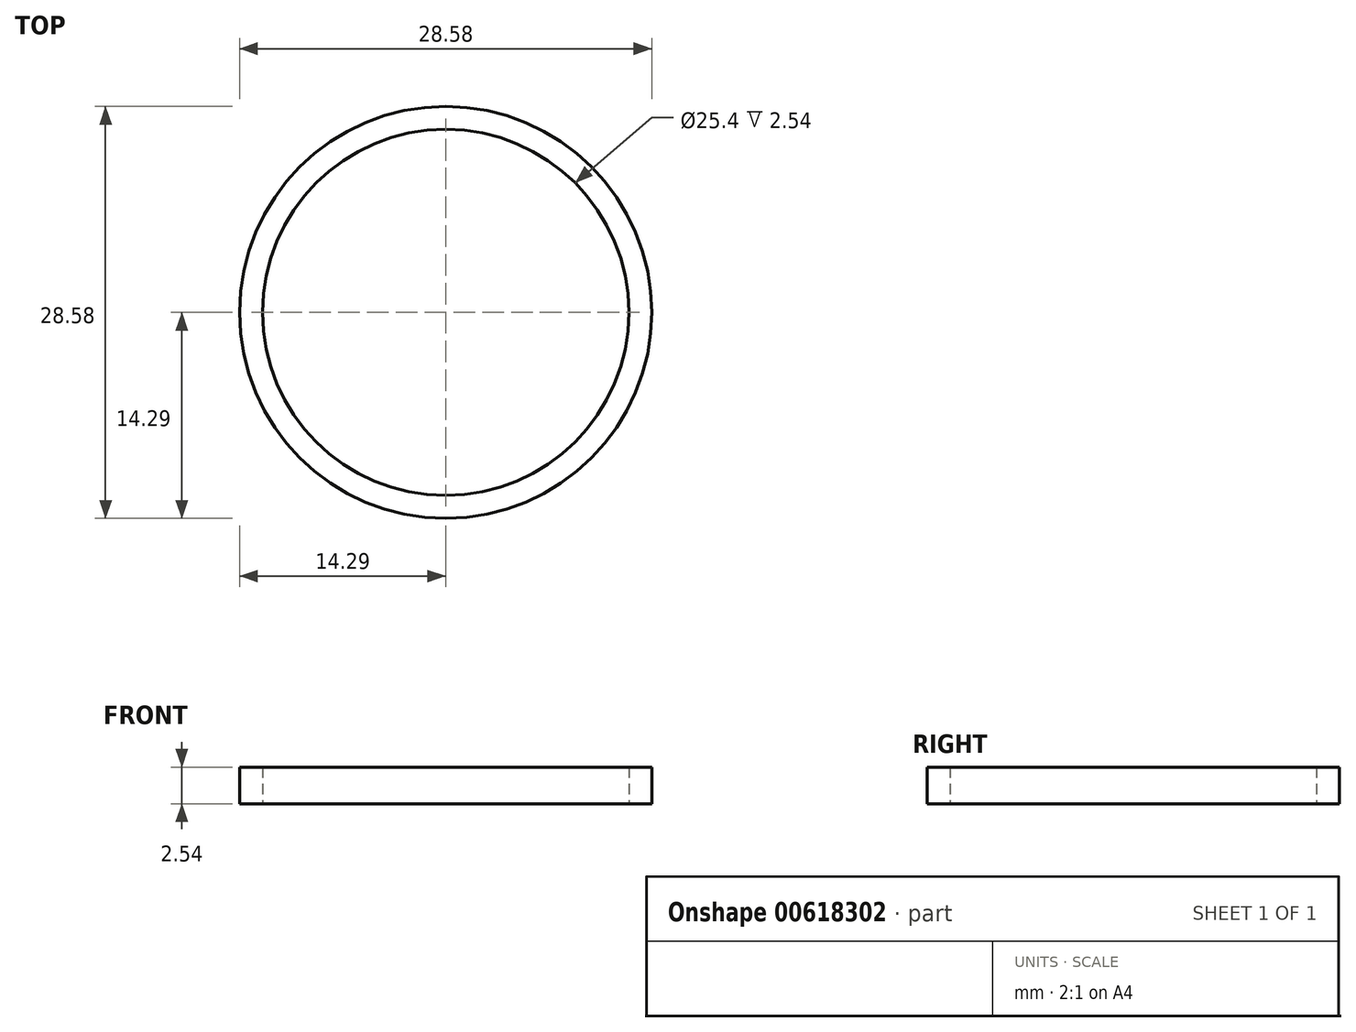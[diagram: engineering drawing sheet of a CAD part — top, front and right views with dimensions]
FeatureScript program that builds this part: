
annotation { "Feature Type Name" : "Feature", "Feature Type Description" : "" }
export const myFeature = defineFeature(function(context is Context, id is Id, definition is map)
    precondition{}
    {
        {
            var Q0;
            Q0=qCreatedBy(makeId("Top.planeOp"),FACE);
            var sketch = newSketch(context, id + "F0", { "sketchPlane" : qUnion([Q0])});
            skLineSegment(sketch, "E0", {"start": v(0, 0) * mm, "end": v(12.7, 0) * mm});
            skCircle(sketch, "E1", {"center": v(0, 0) * mm, "radius": 12.7 * mm});
            skCircle(sketch, "E2.0", {"center": v(0, 0) * mm, "radius": 14.29 * mm});
            skSolve(sketch);
        }
        {
            var Q0;
            Q0=qCreatedBy(makeId("Top.planeOp"),FACE);
            var sketch = newSketch(context, id + "F1", { "sketchPlane" : qUnion([Q0])});
            skSolve(sketch);
        }
        {
            var Q0;
            Q0=qSketchRegion(id+"F1",true);
            var Q1;
            Q1=makeQuery(id+"F0.imprint","IMPRINT",FACE,{"disambiguationData":[TD([[makeQuery(id+"F0.imprint","IMPRINT",EDGE,{"derivedFrom":sQuery(id+"F0.wireOp",EDGE,"E1")}),-1.0]])]});
            extrude(context, id + "F2", {"entities" : qUnion([Q0, Q1]), "depth" : 2.54 * mm, "offsetDistance" : 25.4 * mm});
        }
    });
